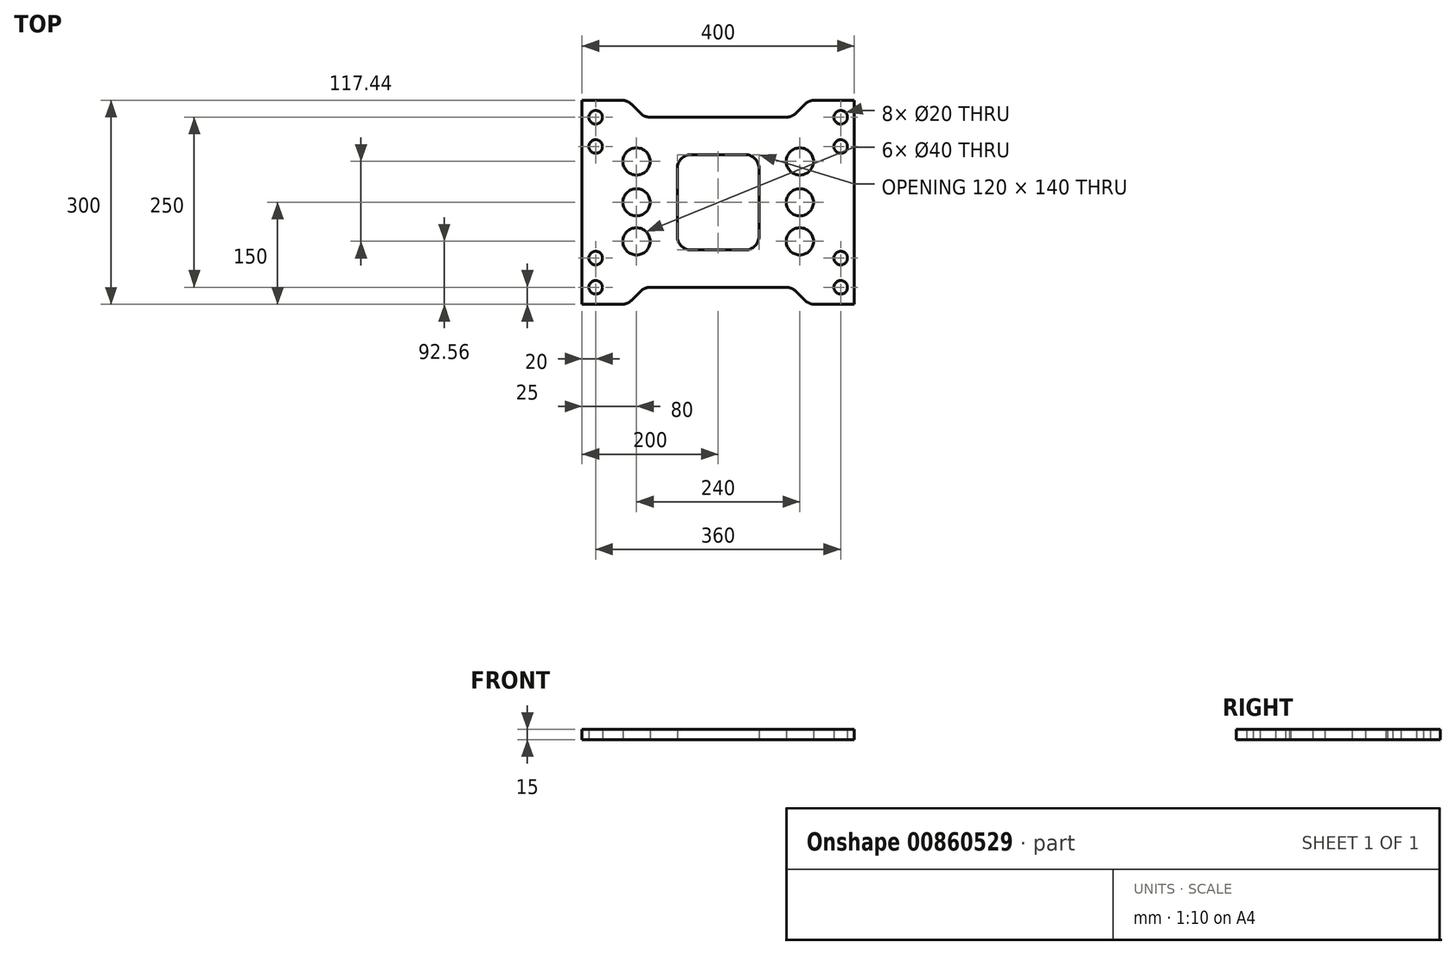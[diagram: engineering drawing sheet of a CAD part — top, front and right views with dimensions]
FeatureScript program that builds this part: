
annotation { "Feature Type Name" : "Feature", "Feature Type Description" : "" }
export const myFeature = defineFeature(function(context is Context, id is Id, definition is map)
    precondition{}
    {
        {
            var Q0;
            Q0=qCreatedBy(makeId("Top.planeOp"),FACE);
            var sketch = newSketch(context, id + "F0", { "sketchPlane" : qUnion([Q0])});
            skCircle(sketch, "E0", {"center": v(-18, 12.5) * mm, "radius": 1 * mm});
            skCircle(sketch, "E1", {"center": v(-18, -12.5) * mm, "radius": 1 * mm});
            skCircle(sketch, "E2", {"center": v(18, 12.5) * mm, "radius": 1 * mm});
            skCircle(sketch, "E3", {"center": v(18, -12.5) * mm, "radius": 1 * mm});
            skCircle(sketch, "E4", {"center": v(-12, 0) * mm, "radius": 2 * mm});
            skCircle(sketch, "E5", {"center": v(-12, 6) * mm, "radius": 2 * mm});
            skCircle(sketch, "E6", {"center": v(-12, -5.74) * mm, "radius": 2 * mm});
            skCircle(sketch, "E7", {"center": v(12, 0) * mm, "radius": 2 * mm});
            skCircle(sketch, "E8", {"center": v(12, 6) * mm, "radius": 2 * mm});
            skCircle(sketch, "E9", {"center": v(12, -5.74) * mm, "radius": 2 * mm});
            skLineSegment(sketch, "E10", {"start": v(-4, 7) * mm, "end": v(4, 7) * mm});
            skArc(sketch, "E11", {"start": v(4, 7) * mm, "mid": v(5.41, 6.41) * mm, "end": v(6, 5) * mm});
            skLineSegment(sketch, "E12", {"start": v(6, 5) * mm, "end": v(6, -5) * mm});
            skArc(sketch, "E13", {"start": v(6, -5) * mm, "mid": v(5.41, -6.41) * mm, "end": v(4, -7) * mm});
            skLineSegment(sketch, "E14", {"start": v(4, -7) * mm, "end": v(-4, -7) * mm});
            skArc(sketch, "E15", {"start": v(-4, -7) * mm, "mid": v(-5.41, -6.41) * mm, "end": v(-6, -5) * mm});
            skLineSegment(sketch, "E16", {"start": v(-6, -5) * mm, "end": v(-6, 5) * mm});
            skArc(sketch, "E17", {"start": v(-6, 5) * mm, "mid": v(-5.41, 6.41) * mm, "end": v(-4, 7) * mm});
            skCircle(sketch, "E18", {"center": v(-18, 8.2) * mm, "radius": 1 * mm});
            skCircle(sketch, "E19", {"center": v(18, 8.2) * mm, "radius": 1 * mm});
            skCircle(sketch, "E20", {"center": v(-18, -8.2) * mm, "radius": 1 * mm});
            skCircle(sketch, "E21", {"center": v(18, -8.2) * mm, "radius": 1 * mm});
            skArc(sketch, "E22", {"start": v(12.74, 14.41) * mm, "mid": v(13.4, 14.85) * mm, "end": v(14.16, 15) * mm});
            skLineSegment(sketch, "E23", {"start": v(14.16, 15) * mm, "end": v(20, 15) * mm});
            skLineSegment(sketch, "E24", {"start": v(20, 15) * mm, "end": v(20, -15) * mm});
            skLineSegment(sketch, "E25", {"start": v(20, -15) * mm, "end": v(14.16, -15) * mm});
            skArc(sketch, "E26", {"start": v(14.16, -15) * mm, "mid": v(13.4, -14.85) * mm, "end": v(12.74, -14.41) * mm});
            skLineSegment(sketch, "E27", {"start": v(12.74, -14.41) * mm, "end": v(11.41, -13.09) * mm});
            skArc(sketch, "E28", {"start": v(11.41, -13.09) * mm, "mid": v(10.77, -12.65) * mm, "end": v(10, -12.5) * mm});
            skLineSegment(sketch, "E29", {"start": v(10, -12.5) * mm, "end": v(-10, -12.5) * mm});
            skArc(sketch, "E30", {"start": v(-10, -12.5) * mm, "mid": v(-10.77, -12.65) * mm, "end": v(-11.41, -13.09) * mm});
            skLineSegment(sketch, "E31", {"start": v(-11.41, -13.09) * mm, "end": v(-12.74, -14.41) * mm});
            skArc(sketch, "E32", {"start": v(-12.74, -14.41) * mm, "mid": v(-13.4, -14.85) * mm, "end": v(-14.16, -15) * mm});
            skLineSegment(sketch, "E33", {"start": v(-14.16, -15) * mm, "end": v(-20, -15) * mm});
            skLineSegment(sketch, "E34", {"start": v(-20, -15) * mm, "end": v(-20, 15) * mm});
            skLineSegment(sketch, "E35", {"start": v(-20, 15) * mm, "end": v(-14.16, 15) * mm});
            skArc(sketch, "E36", {"start": v(-14.16, 15) * mm, "mid": v(-13.4, 14.85) * mm, "end": v(-12.74, 14.41) * mm});
            skLineSegment(sketch, "E37", {"start": v(-12.74, 14.41) * mm, "end": v(-11.41, 13.09) * mm});
            skArc(sketch, "E38", {"start": v(-11.41, 13.09) * mm, "mid": v(-10.77, 12.65) * mm, "end": v(-10, 12.5) * mm});
            skLineSegment(sketch, "E39", {"start": v(-10, 12.5) * mm, "end": v(10, 12.5) * mm});
            skArc(sketch, "E40", {"start": v(10, 12.5) * mm, "mid": v(10.77, 12.65) * mm, "end": v(11.41, 13.09) * mm});
            skLineSegment(sketch, "E41", {"start": v(11.41, 13.09) * mm, "end": v(12.74, 14.41) * mm});
            skSolve(sketch);
        }
        {
            var Q0;
            Q0 = qSketchRegion(id + "F0", true);
            extrude(context, id + "F1", {"entities" : qUnion([Q0]), "depth" : 1.5 * mm, "offsetDistance" : 25 * mm});
        }
        {
            var Q0;
            Q0=makeQuery(id+"F1.opExtrude","SWEPT_BODY",BODY,{"disambiguationData":[OSD([sQuery(id+"F0.wireOp",EDGE,"E0"),sQuery(id+"F0.wireOp",EDGE,"E2"),sQuery(id+"F0.wireOp",EDGE,"E4"),sQuery(id+"F0.wireOp",EDGE,"E5"),sQuery(id+"F0.wireOp",EDGE,"E6"),sQuery(id+"F0.wireOp",EDGE,"E7"),sQuery(id+"F0.wireOp",EDGE,"E8"),sQuery(id+"F0.wireOp",EDGE,"E9"),sQuery(id+"F0.wireOp",EDGE,"E10"),sQuery(id+"F0.wireOp",EDGE,"E11"),sQuery(id+"F0.wireOp",EDGE,"E12"),sQuery(id+"F0.wireOp",EDGE,"E13"),sQuery(id+"F0.wireOp",EDGE,"E14"),sQuery(id+"F0.wireOp",EDGE,"E15"),sQuery(id+"F0.wireOp",EDGE,"E16"),sQuery(id+"F0.wireOp",EDGE,"E17"),sQuery(id+"F0.wireOp",EDGE,"E1"),sQuery(id+"F0.wireOp",EDGE,"E3"),sQuery(id+"F0.wireOp",EDGE,"E18"),sQuery(id+"F0.wireOp",EDGE,"E19"),sQuery(id+"F0.wireOp",EDGE,"E20"),sQuery(id+"F0.wireOp",EDGE,"E21"),sQuery(id+"F0.wireOp",EDGE,"E22"),sQuery(id+"F0.wireOp",EDGE,"E23"),sQuery(id+"F0.wireOp",EDGE,"E24"),sQuery(id+"F0.wireOp",EDGE,"E25"),sQuery(id+"F0.wireOp",EDGE,"E26"),sQuery(id+"F0.wireOp",EDGE,"E27"),sQuery(id+"F0.wireOp",EDGE,"E28"),sQuery(id+"F0.wireOp",EDGE,"E29"),sQuery(id+"F0.wireOp",EDGE,"E30"),sQuery(id+"F0.wireOp",EDGE,"E31"),sQuery(id+"F0.wireOp",EDGE,"E32"),sQuery(id+"F0.wireOp",EDGE,"E33"),sQuery(id+"F0.wireOp",EDGE,"E34"),sQuery(id+"F0.wireOp",EDGE,"E35"),sQuery(id+"F0.wireOp",EDGE,"E36"),sQuery(id+"F0.wireOp",EDGE,"E37"),sQuery(id+"F0.wireOp",EDGE,"E38"),sQuery(id+"F0.wireOp",EDGE,"E39"),sQuery(id+"F0.wireOp",EDGE,"E40"),sQuery(id+"F0.wireOp",EDGE,"E41")])]});
            var Q1;
            Q1=makeQuery(id+"F1.opExtrude","CAP_VERTEX",VERTEX,{"disambiguationData":[OSD([sQuery(id+"F0.wireOp",EDGE,"E33"),sQuery(id+"F0.wireOp",EDGE,"E34")])],"isStart":false});
            transform(context, id + "F2", {"entities" : qUnion([Q0]), "transformType" : TransformType.SCALE_UNIFORMLY, "scale" : 10, "scalePoint" : qUnion([Q1]), "makeCopy" : false});
        }
    });
